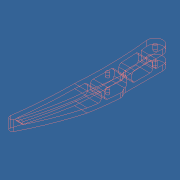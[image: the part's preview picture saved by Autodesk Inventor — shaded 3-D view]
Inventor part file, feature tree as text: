
AUTODESK INVENTOR PART (.ipt)
format: ipt  version: unknown  size: 271,872 bytes
history: native  units: mm
features: extrude x2, sketch x2
ambient origin geometry x8: Origin, YZ Plane, XZ Plane, XY Plane, X Axis, Y Axis, Z Axis, Center Point
feature tree (4):
  extrude  "Выдавливание1"  Depth=1.2mm
  extrude  "Выдавливание2"  Depth=7.5mm TaperAngle=0.0deg
  sketch  "Эскиз1"
  sketch  "Эскиз2"
